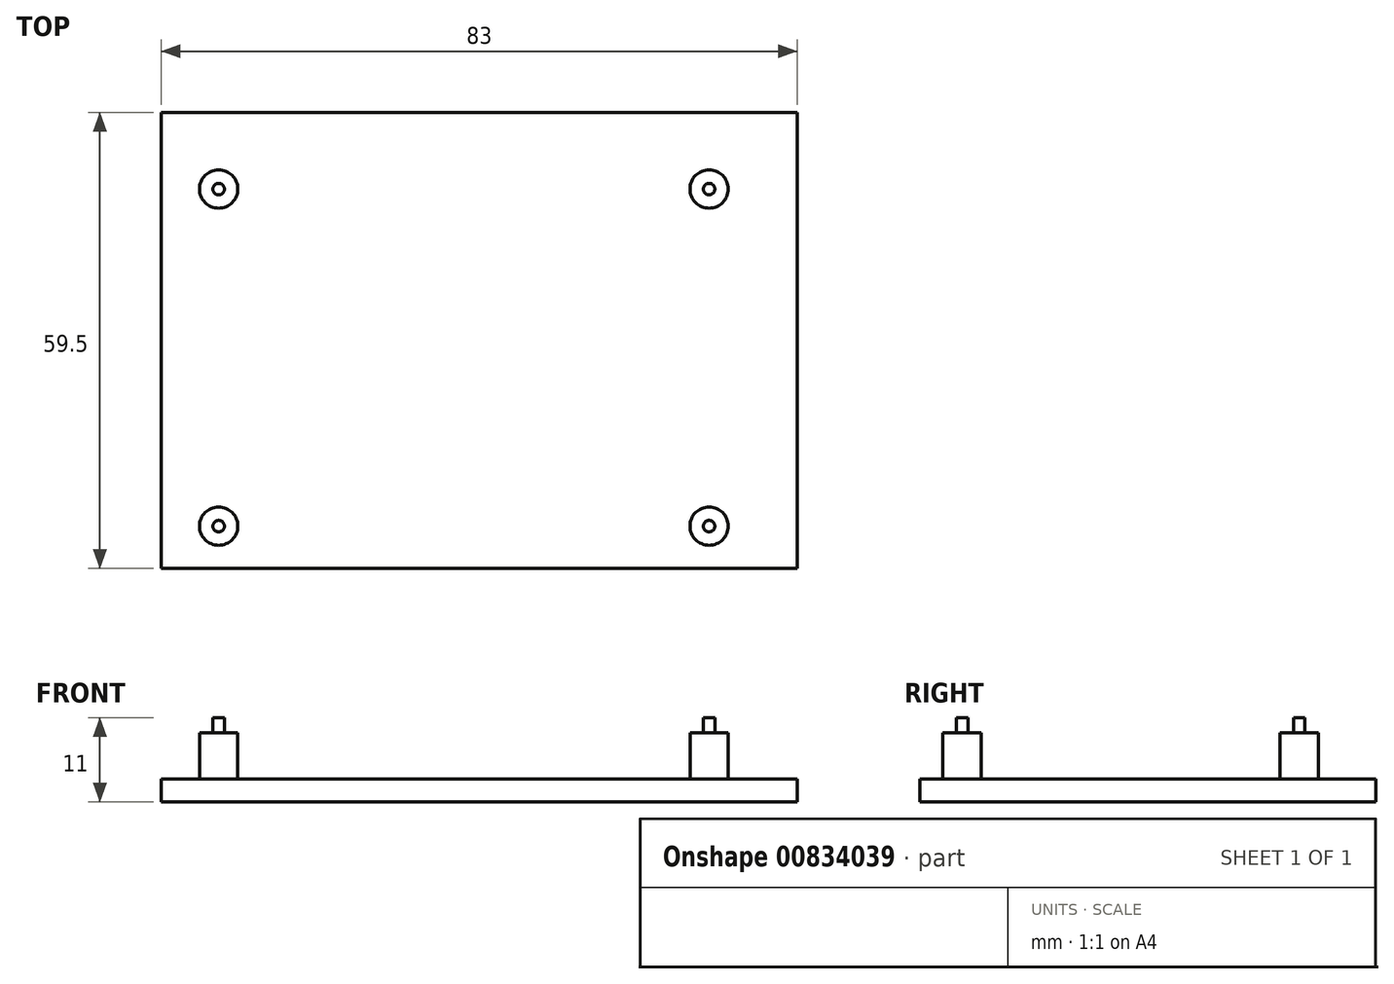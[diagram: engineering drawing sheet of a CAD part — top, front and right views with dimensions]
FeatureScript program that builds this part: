
annotation { "Feature Type Name" : "Feature", "Feature Type Description" : "" }
export const myFeature = defineFeature(function(context is Context, id is Id, definition is map)
    precondition{}
    {
        {
            var Q0;
            Q0=qCreatedBy(makeId("Top.planeOp"),FACE);
            var sketch = newSketch(context, id + "F0", { "sketchPlane" : qUnion([Q0])});
            skLineSegment(sketch, "E0.bottom", {"start": v(-40.96, 36.77) * mm, "end": v(42.04, 36.77) * mm});
            skLineSegment(sketch, "E0.top", {"start": v(-40.96, -22.73) * mm, "end": v(42.04, -22.73) * mm});
            skLineSegment(sketch, "E0.left", {"start": v(-40.96, 36.77) * mm, "end": v(-40.96, -22.73) * mm});
            skLineSegment(sketch, "E0.right", {"start": v(42.04, 36.77) * mm, "end": v(42.04, -22.73) * mm});
            skSolve(sketch);
        }
        {
            var Q0;
            Q0 = qSketchRegion(id + "F0", true);
            extrude(context, id + "F1", {"entities" : qUnion([Q0]), "depth" : 3 * mm, "offsetDistance" : 25.4 * mm});
        }
        {
            var Q0;
            Q0=makeQuery(id+"F1.opExtrude","CAP_FACE",FACE,{"disambiguationData":[OSD([sQuery(id+"F0.wireOp",EDGE,"E0.bottom"),sQuery(id+"F0.wireOp",EDGE,"E0.top"),sQuery(id+"F0.wireOp",EDGE,"E0.left"),sQuery(id+"F0.wireOp",EDGE,"E0.right")])],"isStart":false});
            var sketch = newSketch(context, id + "F2", { "sketchPlane" : qUnion([Q0])});
            skCircle(sketch, "E1", {"center": v(-33.46, 26.77) * mm, "radius": 2.5 * mm});
            skPoint(sketch, "E1.first.point", {"position": v(-35.44, 28.3) * mm});
            skPoint(sketch, "E1.second.point", {"position": v(-31.26, 25.6) * mm});
            skPoint(sketch, "E1.third.point", {"position": v(-32.5, 24.46) * mm});
            skCircle(sketch, "E2", {"center": v(30.54, 26.77) * mm, "radius": 2.5 * mm});
            skPoint(sketch, "E2.first.point", {"position": v(32.8, 27.85) * mm});
            skPoint(sketch, "E2.second.point", {"position": v(32.65, 25.44) * mm});
            skPoint(sketch, "E2.third.point", {"position": v(30.1, 24.3) * mm});
            skCircle(sketch, "E3", {"center": v(-33.46, -17.23) * mm, "radius": 2.5 * mm});
            skPoint(sketch, "E3.first.point", {"position": v(-35.29, -15.52) * mm});
            skPoint(sketch, "E3.second.point", {"position": v(-31.3, -18.47) * mm});
            skPoint(sketch, "E3.third.point", {"position": v(-31.08, -16.48) * mm});
            skCircle(sketch, "E4", {"center": v(30.54, -17.23) * mm, "radius": 2.5 * mm});
            skPoint(sketch, "E4.first.point", {"position": v(30.54, -19.73) * mm});
            skPoint(sketch, "E4.second.point", {"position": v(32.92, -16.48) * mm});
            skPoint(sketch, "E4.third.point", {"position": v(28.15, -16.48) * mm});
            skSolve(sketch);
        }
        {
            var Q0;
            Q0 = qSketchRegion(id + "F2", true);
            extrude(context, id + "F3", {"entities" : qUnion([Q0]), "operationType" : NewBodyOperationType.ADD, "depth" : 6 * mm, "offsetDistance" : 25 * mm});
        }
        {
            var Q0;
            Q0=makeQuery(id+"F1.opExtrude","CAP_FACE",FACE,{"disambiguationData":[OSD([sQuery(id+"F0.wireOp",EDGE,"E0.bottom"),sQuery(id+"F0.wireOp",EDGE,"E0.top"),sQuery(id+"F0.wireOp",EDGE,"E0.left"),sQuery(id+"F0.wireOp",EDGE,"E0.right")])],"isStart":false});
            var sketch = newSketch(context, id + "F4", { "sketchPlane" : qUnion([Q0])});
            skCircle(sketch, "E5", {"center": v(-33.46, 26.77) * mm, "radius": 0.75 * mm});
            skCircle(sketch, "E6", {"center": v(30.54, 26.77) * mm, "radius": 0.75 * mm});
            skCircle(sketch, "E7", {"center": v(30.54, -17.23) * mm, "radius": 0.75 * mm});
            skCircle(sketch, "E8", {"center": v(-33.46, -17.23) * mm, "radius": 0.75 * mm});
            skSolve(sketch);
        }
        {
            var Q0;
            Q0 = qSketchRegion(id + "F4", true);
            extrude(context, id + "F5", {"entities" : qUnion([Q0]), "operationType" : NewBodyOperationType.ADD, "depth" : 8 * mm, "offsetDistance" : 25 * mm});
        }
    });
